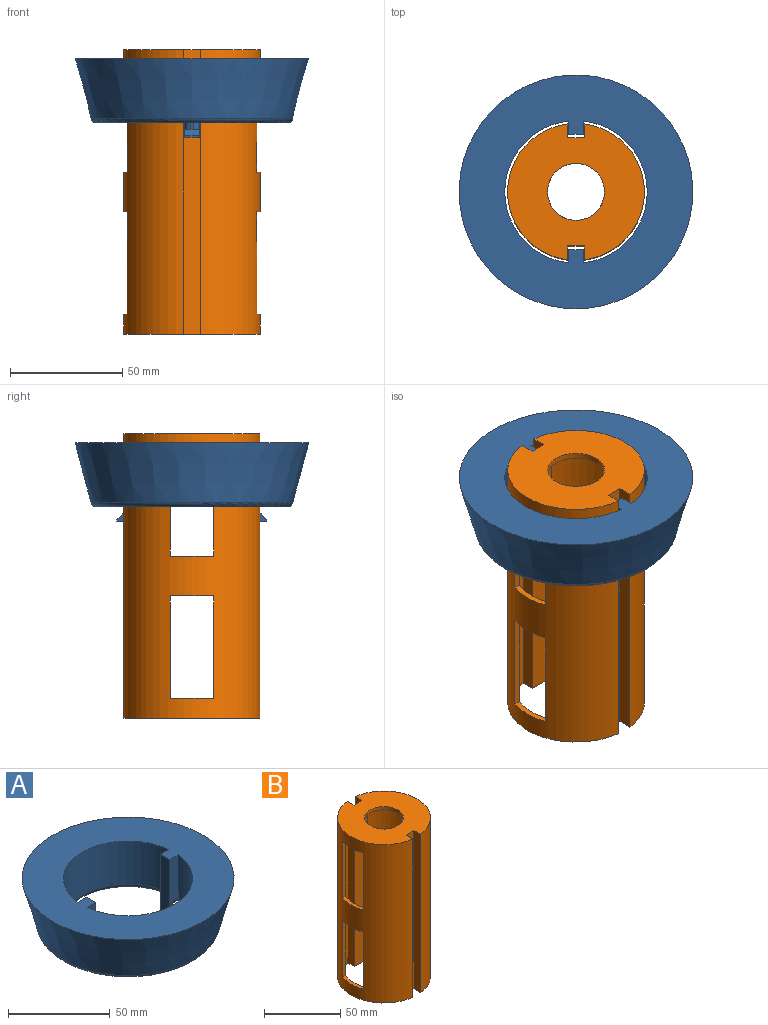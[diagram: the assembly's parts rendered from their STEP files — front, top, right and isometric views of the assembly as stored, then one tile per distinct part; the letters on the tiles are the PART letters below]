
ASSEMBLY  parts=2 mates=1
PART A: 50 faces, bbox 104.2x104.2x34.9 mm
  f0: plane 85x85mm, normal (0,0,-1), area 1994.6mm2, adj f10,f12,f21,f22,f23,f26,f27,f28
  f1: plane 34.93x6.35mm, normal (1,0,0), area 221.8mm2, adj f2,f9,f11,f31
  f2: plane 34.93x7.75mm, normal (0,1,0), area 178.4mm2, adj f1,f3,f11,f14,f15,f19,f25,f26
  f3: cylinder r=31.75mm len=63.18mm, axis (0,0,-1), area 2431.3mm2, adj f2,f4,f27,f31
  f4: plane 34.93x7.75mm, normal (0,1,0), area 178.4mm2, adj f3,f5,f13,f16,f17,f18,f28,f29
  f5: plane 34.93x6.35mm, normal (-1,0,0), area 221.8mm2, adj f4,f6,f13,f31
  f6: plane 34.93x7.75mm, normal (0,-1,0), area 178.4mm2, adj f5,f7,f13,f16,f17,f18,f23,f24
  f7: cylinder r=31.75mm len=63.18mm, axis (0,0,-1), area 2431.3mm2, adj f6,f9,f22,f31
  f8: cone r=44.45mm half-angle=15deg, axis (0,0,1), area 8426.3mm2, adj f30,f31
  f9: plane 34.93x7.75mm, normal (0,-1,0), area 178.4mm2, adj f1,f7,f11,f14,f15,f19,f20,f21
  f10: plane 3.18x1.27mm, normal (-1,0,0), area 4mm2, adj f0,f14,f20,f25
  f11: plane 7.75x6.35mm, normal (0,0,-1), area 49.2mm2, adj f1,f2,f9,f15
  f12: plane 3.18x1.27mm, normal (1,0,0), area 4mm2, adj f0,f16,f24,f29
  f13: plane 7.75x6.35mm, normal (0,0,-1), area 49.2mm2, adj f4,f5,f6,f17
  f14: plane 6.35x4.57mm, normal (0,0,1), area 15.7mm2, adj f2,f9,f10,f19,f20,f25
  f15: plane 6.35x0.64mm, normal (-1,0,0), area 4mm2, adj f2,f9,f11,f19
  f16: plane 6.35x4.57mm, normal (0,0,1), area 15.7mm2, adj f4,f6,f12,f18,f24,f29
  f17: plane 6.35x0.64mm, normal (1,0,0), area 4mm2, adj f4,f6,f13,f18
  f18: plane 6.35x2.54mm, normal (0.71,0,0.71), area 22.8mm2, adj f4,f6,f16,f17
  f19: plane 6.35x2.54mm, normal (-0.71,0,0.71), area 22.8mm2, adj f2,f9,f14,f15
  f20: cylinder r=2.54mm len=5.72mm, axis (0,0,-1), area 16.4mm2, adj f9,f10,f14,f21
  f21: cylinder r=2.54mm len=7.95mm, axis (1,0,0), area 18.5mm2, adj f0,f9,f20,f22
  f22: torus R=34.29mm, axis (0,0,1), area 391.5mm2, adj f0,f7,f21,f23
  f23: cylinder r=2.54mm len=7.95mm, axis (1,0,0), area 18.5mm2, adj f0,f6,f22,f24
  f24: cylinder r=2.54mm len=5.72mm, axis (0,0,-1), area 16.4mm2, adj f6,f12,f16,f23
  f25: cylinder r=2.54mm len=5.72mm, axis (0,0,1), area 16.4mm2, adj f2,f10,f14,f26
  f26: cylinder r=2.54mm len=7.95mm, axis (-1,0,0), area 18.5mm2, adj f0,f2,f25,f27
  f27: torus R=34.29mm, axis (0,0,1), area 391.5mm2, adj f0,f3,f26,f28
  f28: cylinder r=2.54mm len=7.95mm, axis (-1,0,0), area 18.5mm2, adj f0,f4,f27,f29
  f29: cylinder r=2.54mm len=5.72mm, axis (0,0,1), area 16.4mm2, adj f4,f12,f16,f28
  f30: torus R=42.5mm, axis (0,0,1), area 917.9mm2, adj f0,f8
  f31: plane 104.21x104.21mm, normal (0,0,1), area 5439mm2, adj f1,f2,f3,f4,f5,f6,f7,f8
  f32: plane 24.51x2.29mm, normal (-1,0,0), area 55.9mm2, adj f33,f34,f41,f42,f45,f49
  f33: plane 83.82x83.82mm, normal (0,0,1), area 1840.8mm2, adj f32,f37,f42,f43,f44,f45,f46,f47
  f34: plane 24x6.03mm, normal (0,-1,0), area 144.8mm2, adj f32,f35,f45,f49
  f35: cylinder r=33.78mm len=67.53mm, axis (0,0,-1), area 2492.5mm2, adj f34,f36,f46,f49
  f36: plane 24x6.03mm, normal (0,-1,0), area 144.8mm2, adj f35,f37,f47,f49
  f37: plane 24.51x2.29mm, normal (1,0,0), area 55.9mm2, adj f33,f36,f38,f44,f47,f49
  f38: plane 24x6.03mm, normal (0,1,0), area 144.8mm2, adj f37,f39,f44,f49
  f39: cylinder r=33.78mm len=67.53mm, axis (0,0,-1), area 2492.5mm2, adj f38,f41,f43,f49
  f40: cylinder r=42.42mm len=84.84mm, axis (0,0,-1), area 6397.3mm2, adj f48,f49
  f41: plane 24x6.03mm, normal (0,1,0), area 144.8mm2, adj f32,f39,f42,f49
  f42: cylinder r=0.51mm len=6.55mm, axis (1,0,0), area 5mm2, adj f32,f33,f41,f43
  f43: torus R=34.29mm, axis (0,0,1), area 83.6mm2, adj f33,f39,f42,f44
  f44: cylinder r=0.51mm len=6.55mm, axis (1,0,0), area 5mm2, adj f33,f37,f38,f43
  f45: cylinder r=0.51mm len=6.55mm, axis (-1,0,0), area 5mm2, adj f32,f33,f34,f46
  f46: torus R=34.29mm, axis (0,0,1), area 83.6mm2, adj f33,f35,f45,f47
  f47: cylinder r=0.51mm len=6.55mm, axis (-1,0,0), area 5mm2, adj f33,f36,f37,f46
  f48: torus R=41.91mm, axis (0,0,1), area 211.7mm2, adj f33,f40
  f49: plane 84.84x84.84mm, normal (0,0,-1), area 2095mm2, adj f32,f34,f35,f36,f37,f38,f39,f40
PART B: 36 faces, bbox 61x60.5x127 mm
  f0: cylinder r=30.48mm len=127mm, axis (0,0,-1), area 9450.3mm2, adj f4,f5,f7,f10,f27,f28,f29,f30
  f1: cylinder r=30.48mm len=127mm, axis (0,0,-1), area 9450.3mm2, adj f4,f5,f6,f11,f19,f20,f21,f22
  f2: cylinder r=27.94mm len=124.46mm, axis (0,0,-1), area 7583.3mm2, adj f5,f12,f14,f17,f27,f28,f29,f30
  f3: cylinder r=27.94mm len=124.46mm, axis (0,0,-1), area 7583.3mm2, adj f5,f12,f13,f18,f19,f20,f21,f22
  f4: plane 60.96x60.53mm, normal (0,0,1), area 2320.9mm2, adj f0,f1,f6,f7,f8,f9,f10,f11
  f5: plane 60.96x60.53mm, normal (0,0,-1), area 526.6mm2, adj f0,f1,f2,f3,f6,f7,f8,f9
  f6: plane 127x6.18mm, normal (1,0,0), area 785.3mm2, adj f1,f4,f5,f8
  f7: plane 127x6.18mm, normal (-1,0,0), area 785.3mm2, adj f0,f4,f5,f8
  f8: plane 127x7.19mm, normal (0,-1,0), area 913.6mm2, adj f4,f5,f6,f7
  f9: plane 127x7.19mm, normal (0,1,0), area 913.6mm2, adj f4,f5,f10,f11
  f10: plane 127x6.18mm, normal (-1,0,0), area 785.3mm2, adj f0,f4,f5,f9
  f11: plane 127x6.18mm, normal (1,0,0), area 785.3mm2, adj f1,f4,f5,f9
  f12: plane 55.88x54.52mm, normal (0,0,-1), area 1794.3mm2, adj f2,f3,f13,f14,f15,f16,f17,f18
  f13: plane 124.46x5.71mm, normal (-1,0,0), area 711.2mm2, adj f3,f5,f12,f15
  f14: plane 124.46x5.71mm, normal (1,0,0), area 711.2mm2, adj f2,f5,f12,f15
  f15: plane 124.46x12.27mm, normal (0,1,0), area 1527.6mm2, adj f5,f12,f13,f14
  f16: plane 124.46x12.27mm, normal (0,-1,0), area 1527.6mm2, adj f5,f12,f17,f18
  f17: plane 124.46x5.71mm, normal (1,0,0), area 711.2mm2, adj f2,f5,f12,f16
  f18: plane 124.46x5.71mm, normal (-1,0,0), area 711.2mm2, adj f3,f5,f12,f16
  f19: plane 19.3x4.26mm, normal (0,0,1), area 50mm2, adj f1,f3,f20,f22
  f20: plane 45.69x2.69mm, normal (0,1,0), area 123mm2, adj f1,f3,f19,f21
  f21: plane 19.3x4.26mm, normal (0,0,-1), area 50mm2, adj f1,f3,f20,f22
  f22: plane 45.69x2.69mm, normal (0,-1,0), area 123mm2, adj f1,f3,f19,f21
  f23: plane 45.69x2.69mm, normal (0,1,0), area 123mm2, adj f1,f3,f24,f26
  f24: plane 19.3x4.26mm, normal (0,0,-1), area 50mm2, adj f1,f3,f23,f25
  f25: plane 45.69x2.69mm, normal (0,-1,0), area 123mm2, adj f1,f3,f24,f26
  f26: plane 19.3x4.26mm, normal (0,0,1), area 50mm2, adj f1,f3,f23,f25
  f27: plane 45.69x2.69mm, normal (0,-1,0), area 123mm2, adj f0,f2,f28,f30
  f28: plane 19.3x4.26mm, normal (0,0,-1), area 50mm2, adj f0,f2,f27,f29
  f29: plane 45.69x2.69mm, normal (0,1,0), area 123mm2, adj f0,f2,f28,f30
  f30: plane 19.3x4.26mm, normal (0,0,1), area 50mm2, adj f0,f2,f27,f29
  f31: plane 19.3x4.26mm, normal (0,0,1), area 50mm2, adj f0,f2,f32,f34
  f32: plane 45.69x2.69mm, normal (0,-1,0), area 123mm2, adj f0,f2,f31,f33
  f33: plane 19.3x4.26mm, normal (0,0,-1), area 50mm2, adj f0,f2,f32,f34
  f34: plane 45.69x2.69mm, normal (0,1,0), area 123mm2, adj f0,f2,f31,f33
  f35: cylinder r=12.7mm len=25.4mm, axis (0,0,-1), area 202.7mm2, adj f4,f12
PLACE A rot(axis=(0,0,-1),90deg) t=(-58.18,-20.12,94.32)mm
PLACE B t=(-58.18,-20.12,0)mm
MATE slider A.f3 <-> B.f0  axis (0,0,-1) through (-58.18,-20.12,122.9)mm
